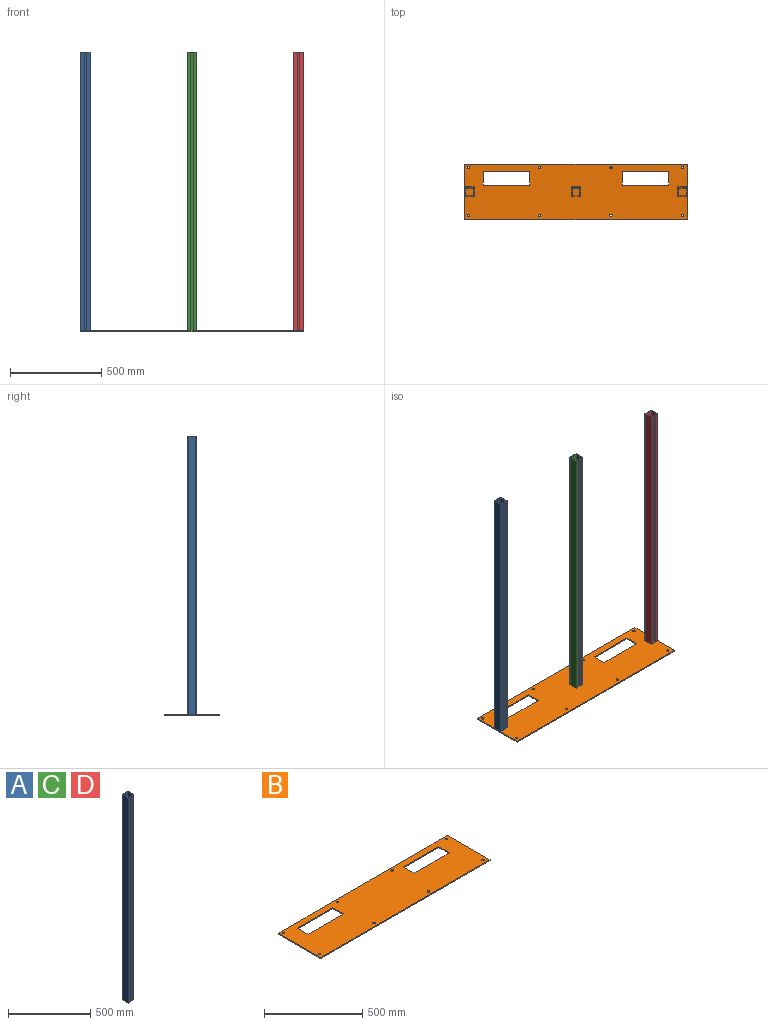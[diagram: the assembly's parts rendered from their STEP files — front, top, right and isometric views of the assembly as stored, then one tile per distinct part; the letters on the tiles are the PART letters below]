
ASSEMBLY  parts=4 mates=1
PART A: 14 faces, bbox 50.8x50.8x1524 mm
  f0: plane 1524x4.57mm, normal (1,0,0), area 6967.7mm2, adj f1,f11,f12,f13
  f1: plane 1524x14.48mm, normal (0,1,0), area 22064.5mm2, adj f0,f2,f12,f13
  f2: plane 1524x41.66mm, normal (1,0,0), area 63483.7mm2, adj f1,f3,f12,f13
  f3: plane 1524x41.66mm, normal (0,-1,0), area 63483.7mm2, adj f2,f4,f12,f13
  f4: plane 1524x41.66mm, normal (-1,0,0), area 63483.7mm2, adj f3,f5,f12,f13
  f5: plane 1524x14.48mm, normal (0,1,0), area 22064.5mm2, adj f4,f6,f12,f13
  f6: plane 1524x4.57mm, normal (-1,0,0), area 6967.7mm2, adj f5,f7,f12,f13
  f7: plane 1524x19.05mm, normal (0,-1,0), area 29032.2mm2, adj f6,f8,f12,f13
  f8: plane 1524x50.8mm, normal (1,0,0), area 77419.2mm2, adj f7,f9,f12,f13
  f9: plane 1524x50.8mm, normal (0,1,0), area 77419.2mm2, adj f8,f10,f12,f13
  f10: plane 1524x50.8mm, normal (-1,0,0), area 77419.2mm2, adj f9,f11,f12,f13
  f11: plane 1524x19.05mm, normal (0,-1,0), area 29032.2mm2, adj f0,f10,f12,f13
  f12: plane 50.8x50.8mm, normal (0,0,1), area 787.4mm2, adj f0,f1,f2,f3,f4,f5,f6,f7
  f13: plane 50.8x50.8mm, normal (0,0,-1), area 787.4mm2, adj f0,f1,f2,f3,f4,f5,f6,f7
PART B: 22 faces, bbox 1219.2x304.8x6.1 mm
  f0: plane 1219.2x304.8mm, normal (0,0,1), area 331889.1mm2, adj f2,f3,f4,f5,f6,f7,f8,f9
  f1: plane 1219.2x304.8mm, normal (0,0,-1), area 331889.1mm2, adj f2,f3,f4,f5,f6,f7,f8,f9
  f2: plane 1219.2x6.1mm, normal (0,-1,0), area 7432.2mm2, adj f0,f1,f3,f13
  f3: plane 304.8x6.1mm, normal (1,0,0), area 1858.1mm2, adj f0,f1,f2,f4
  f4: plane 1219.2x6.1mm, normal (0,1,0), area 7432.2mm2, adj f0,f1,f3,f13
  f5: cylinder r=6.35mm len=12.7mm, axis (0,0,-1), area 243.2mm2, adj f0,f1
  f6: cylinder r=6.35mm len=12.7mm, axis (0,0,-1), area 243.2mm2, adj f0,f1
  f7: cylinder r=6.35mm len=12.7mm, axis (0,0,-1), area 243.2mm2, adj f0,f1
  f8: cylinder r=6.35mm len=12.7mm, axis (0,0,-1), area 243.2mm2, adj f0,f1
  f9: cylinder r=6.35mm len=12.7mm, axis (0,0,-1), area 243.2mm2, adj f0,f1
  f10: cylinder r=6.35mm len=12.7mm, axis (0,0,-1), area 243.2mm2, adj f0,f1
  f11: cylinder r=6.35mm len=12.7mm, axis (0,0,-1), area 243.2mm2, adj f0,f1
  f12: cylinder r=6.35mm len=12.7mm, axis (0,0,-1), area 243.2mm2, adj f0,f1
  f13: plane 304.8x6.1mm, normal (-1,0,0), area 1858.1mm2, adj f0,f1,f2,f4
  f14: plane 254x6.1mm, normal (0,-1,0), area 1548.4mm2, adj f0,f1,f15,f17
  f15: plane 76.2x6.1mm, normal (1,0,0), area 464.5mm2, adj f0,f1,f14,f16
  f16: plane 254x6.1mm, normal (0,1,0), area 1548.4mm2, adj f0,f1,f15,f17
  f17: plane 76.2x6.1mm, normal (-1,0,0), area 464.5mm2, adj f0,f1,f14,f16
  f18: plane 254x6.1mm, normal (0,-1,0), area 1548.4mm2, adj f0,f1,f19,f21
  f19: plane 76.2x6.1mm, normal (1,0,0), area 464.5mm2, adj f0,f1,f18,f20
  f20: plane 254x6.1mm, normal (0,1,0), area 1548.4mm2, adj f0,f1,f19,f21
  f21: plane 76.2x6.1mm, normal (-1,0,0), area 464.5mm2, adj f0,f1,f18,f20
PART C: same geometry as A
PART D: same geometry as A
PLACE A t=(-1219.2,127,6.1)mm
PLACE B t=(-609.6,152.4,0)mm
PLACE C t=(-635,127,6.1)mm
PLACE D t=(-50.8,127,6.1)mm
MATE fastened A.f13 <-> B.f0  axis (0,0,-1) through (-1219.2,152.4,6.1)mm
